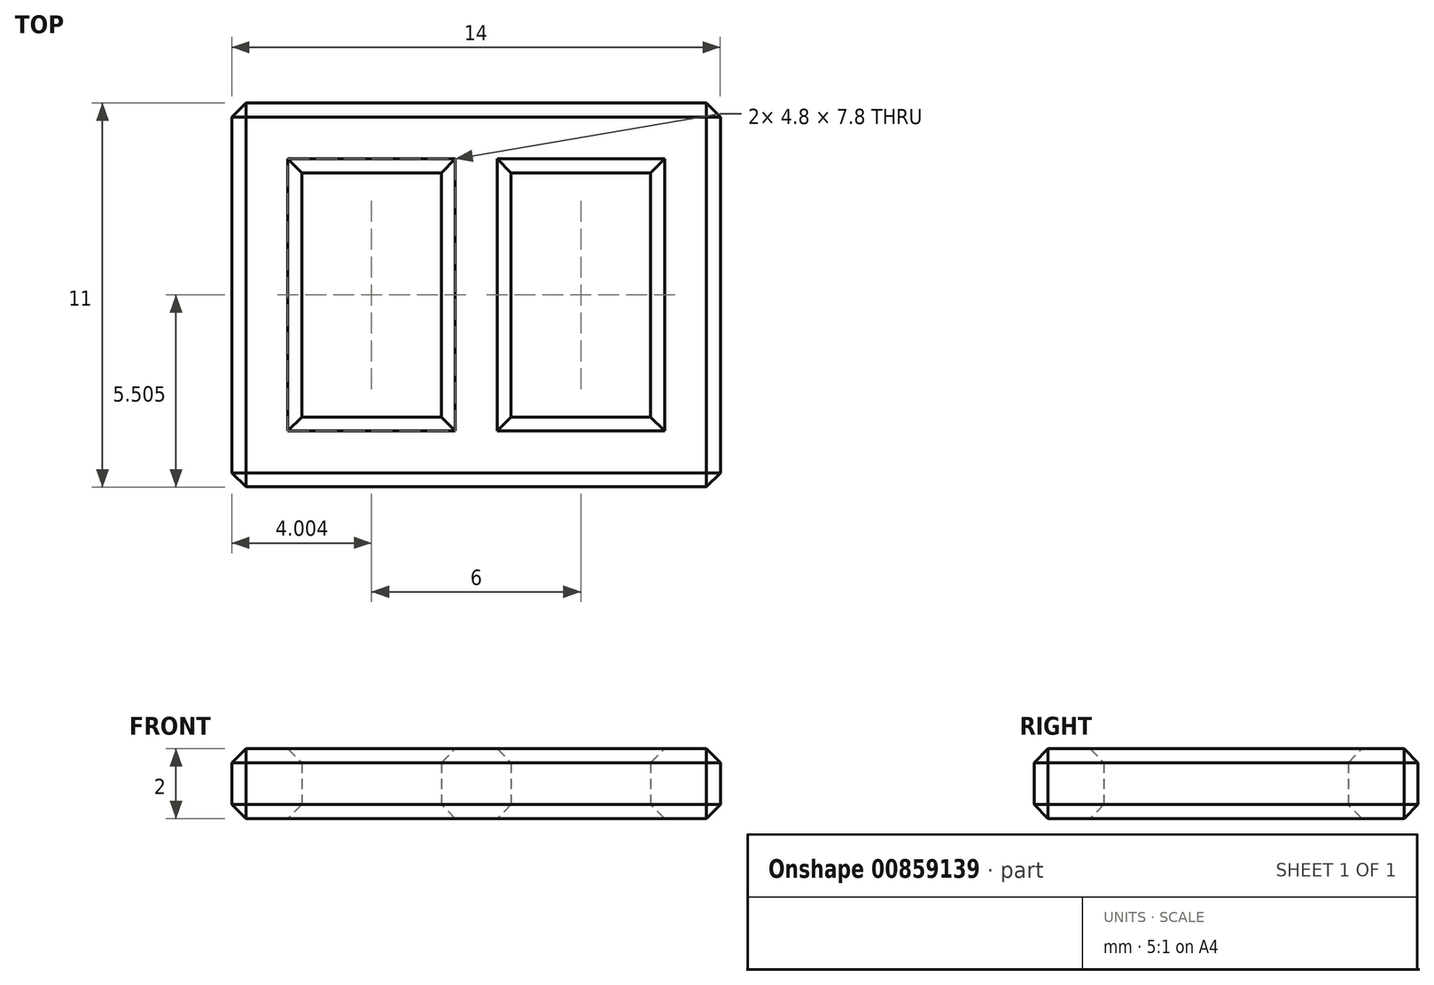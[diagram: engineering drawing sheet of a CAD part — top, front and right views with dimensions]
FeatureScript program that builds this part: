
annotation { "Feature Type Name" : "Feature", "Feature Type Description" : "" }
export const myFeature = defineFeature(function(context is Context, id is Id, definition is map)
    precondition{}
    {
        {
            var Q0;
            Q0=qCreatedBy(makeId("Top.planeOp"),FACE);
            var sketch = newSketch(context, id + "F0", { "sketchPlane" : qUnion([Q0])});
            skLineSegment(sketch, "E0", {"start": v(-3.9, 7.11) * mm, "end": v(-3.9, -3.89) * mm});
            skLineSegment(sketch, "E1", {"start": v(-3.9, -3.89) * mm, "end": v(10.1, -3.89) * mm});
            skLineSegment(sketch, "E2", {"start": v(10.1, -3.89) * mm, "end": v(10.1, 7.11) * mm});
            skLineSegment(sketch, "E3", {"start": v(10.1, 7.11) * mm, "end": v(-3.9, 7.11) * mm});
            skLineSegment(sketch, "E4.bottom", {"start": v(-1.9, 5.11) * mm, "end": v(2.1, 5.11) * mm});
            skLineSegment(sketch, "E4.top", {"start": v(-1.9, -1.89) * mm, "end": v(2.1, -1.89) * mm});
            skLineSegment(sketch, "E4.left", {"start": v(-1.9, 5.11) * mm, "end": v(-1.9, -1.89) * mm});
            skLineSegment(sketch, "E4.right", {"start": v(2.1, 5.11) * mm, "end": v(2.1, -1.89) * mm});
            skPoint(sketch, "E5.firstSnap0", {"position": v(0.1, 5.11) * mm});
            skLineSegment(sketch, "E5.bottom", {"start": v(4.1, 5.11) * mm, "end": v(8.1, 5.11) * mm});
            skLineSegment(sketch, "E5.top", {"start": v(4.1, -1.89) * mm, "end": v(8.1, -1.89) * mm});
            skLineSegment(sketch, "E5.left", {"start": v(4.1, 5.11) * mm, "end": v(4.1, -1.89) * mm});
            skLineSegment(sketch, "E5.right", {"start": v(8.1, 5.11) * mm, "end": v(8.1, -1.89) * mm});
            skSolve(sketch);
        }
        {
            var Q0;
            Q0 = qSketchRegion(id + "F0", true);
            extrude(context, id + "F1", {"entities" : qUnion([Q0]), "depth" : 2 * mm, "offsetDistance" : 25 * mm});
        }
        {
            var Q0;
            Q0=makeQuery(id+"F1.opExtrude","CAP_EDGE",EDGE,{"disambiguationData":[OSD([sQuery(id+"F0.wireOp",EDGE,"E1")])],"isStart":false});
            var Q1;
            Q1=makeQuery(id+"F1.opExtrude","CAP_EDGE",EDGE,{"disambiguationData":[OSD([sQuery(id+"F0.wireOp",EDGE,"E0")])],"isStart":false});
            var Q2;
            Q2=makeQuery(id+"F1.opExtrude","CAP_EDGE",EDGE,{"disambiguationData":[OSD([sQuery(id+"F0.wireOp",EDGE,"E4.left")])],"isStart":false});
            var Q3;
            Q3=makeQuery(id+"F1.opExtrude","CAP_EDGE",EDGE,{"disambiguationData":[OSD([sQuery(id+"F0.wireOp",EDGE,"E4.right")])],"isStart":false});
            var Q4;
            Q4=makeQuery(id+"F1.opExtrude","CAP_EDGE",EDGE,{"disambiguationData":[OSD([sQuery(id+"F0.wireOp",EDGE,"E5.left")])],"isStart":false});
            var Q5;
            Q5=makeQuery(id+"F1.opExtrude","CAP_EDGE",EDGE,{"disambiguationData":[OSD([sQuery(id+"F0.wireOp",EDGE,"E5.right")])],"isStart":false});
            var Q6;
            Q6=makeQuery(id+"F1.opExtrude","CAP_EDGE",EDGE,{"disambiguationData":[OSD([sQuery(id+"F0.wireOp",EDGE,"E4.bottom")])],"isStart":false});
            var Q7;
            Q7=makeQuery(id+"F1.opExtrude","CAP_EDGE",EDGE,{"disambiguationData":[OSD([sQuery(id+"F0.wireOp",EDGE,"E4.top")])],"isStart":false});
            var Q8;
            Q8=makeQuery(id+"F1.opExtrude","CAP_EDGE",EDGE,{"disambiguationData":[OSD([sQuery(id+"F0.wireOp",EDGE,"E5.top")])],"isStart":false});
            var Q9;
            Q9=makeQuery(id+"F1.opExtrude","CAP_EDGE",EDGE,{"disambiguationData":[OSD([sQuery(id+"F0.wireOp",EDGE,"E2")])],"isStart":false});
            var Q10;
            Q10=makeQuery(id+"F1.opExtrude","CAP_EDGE",EDGE,{"disambiguationData":[OSD([sQuery(id+"F0.wireOp",EDGE,"E3")])],"isStart":false});
            var Q11;
            Q11=makeQuery(id+"F1.opExtrude","CAP_EDGE",EDGE,{"disambiguationData":[OSD([sQuery(id+"F0.wireOp",EDGE,"E5.bottom")])],"isStart":false});
            var Q12;
            Q12=makeQuery(id+"F1.opExtrude","SWEPT_EDGE",EDGE,{"disambiguationData":[OSD([sQuery(id+"F0.wireOp",EDGE,"E2"),sQuery(id+"F0.wireOp",EDGE,"E3")])]});
            var Q13;
            Q13=makeQuery(id+"F1.opExtrude","SWEPT_EDGE",EDGE,{"disambiguationData":[OSD([sQuery(id+"F0.wireOp",EDGE,"E0"),sQuery(id+"F0.wireOp",EDGE,"E3")])]});
            var Q14;
            Q14=makeQuery(id+"F1.opExtrude","SWEPT_EDGE",EDGE,{"disambiguationData":[OSD([sQuery(id+"F0.wireOp",EDGE,"E1"),sQuery(id+"F0.wireOp",EDGE,"E2")])]});
            var Q15;
            Q15=makeQuery(id+"F1.opExtrude","SWEPT_EDGE",EDGE,{"disambiguationData":[OSD([sQuery(id+"F0.wireOp",EDGE,"E0"),sQuery(id+"F0.wireOp",EDGE,"E1")])]});
            var Q16;
            Q16=makeQuery(id+"F1.opExtrude","CAP_EDGE",EDGE,{"disambiguationData":[OSD([sQuery(id+"F0.wireOp",EDGE,"E1")])],"isStart":true});
            var Q17;
            Q17=makeQuery(id+"F1.opExtrude","CAP_EDGE",EDGE,{"disambiguationData":[OSD([sQuery(id+"F0.wireOp",EDGE,"E2")])],"isStart":true});
            var Q18;
            Q18=makeQuery(id+"F1.opExtrude","CAP_EDGE",EDGE,{"disambiguationData":[OSD([sQuery(id+"F0.wireOp",EDGE,"E5.right")])],"isStart":true});
            var Q19;
            Q19=makeQuery(id+"F1.opExtrude","CAP_EDGE",EDGE,{"disambiguationData":[OSD([sQuery(id+"F0.wireOp",EDGE,"E5.bottom")])],"isStart":true});
            var Q20;
            Q20=makeQuery(id+"F1.opExtrude","CAP_EDGE",EDGE,{"disambiguationData":[OSD([sQuery(id+"F0.wireOp",EDGE,"E5.left")])],"isStart":true});
            var Q21;
            Q21=makeQuery(id+"F1.opExtrude","CAP_EDGE",EDGE,{"disambiguationData":[OSD([sQuery(id+"F0.wireOp",EDGE,"E5.top")])],"isStart":true});
            var Q22;
            Q22=makeQuery(id+"F1.opExtrude","CAP_EDGE",EDGE,{"disambiguationData":[OSD([sQuery(id+"F0.wireOp",EDGE,"E4.right")])],"isStart":true});
            var Q23;
            Q23=makeQuery(id+"F1.opExtrude","CAP_EDGE",EDGE,{"disambiguationData":[OSD([sQuery(id+"F0.wireOp",EDGE,"E4.bottom")])],"isStart":true});
            var Q24;
            Q24=makeQuery(id+"F1.opExtrude","CAP_EDGE",EDGE,{"disambiguationData":[OSD([sQuery(id+"F0.wireOp",EDGE,"E4.top")])],"isStart":true});
            var Q25;
            Q25=makeQuery(id+"F1.opExtrude","CAP_EDGE",EDGE,{"disambiguationData":[OSD([sQuery(id+"F0.wireOp",EDGE,"E4.left")])],"isStart":true});
            var Q26;
            Q26=makeQuery(id+"F1.opExtrude","CAP_EDGE",EDGE,{"disambiguationData":[OSD([sQuery(id+"F0.wireOp",EDGE,"E0")])],"isStart":true});
            var Q27;
            Q27=makeQuery(id+"F1.opExtrude","CAP_EDGE",EDGE,{"disambiguationData":[OSD([sQuery(id+"F0.wireOp",EDGE,"E3")])],"isStart":true});
            chamfer(context, id + "F2", {"entities" : qUnion([Q0, Q1, Q2, Q3, Q4, Q5, Q6, Q7, Q8, Q9, Q10, Q11, Q12, Q13, Q14, Q15, Q16, Q17, Q18, Q19, Q20, Q21, Q22, Q23, Q24, Q25, Q26, Q27]), "width" : .4 * mm, "tangentPropagation" : true});
        }
    });
